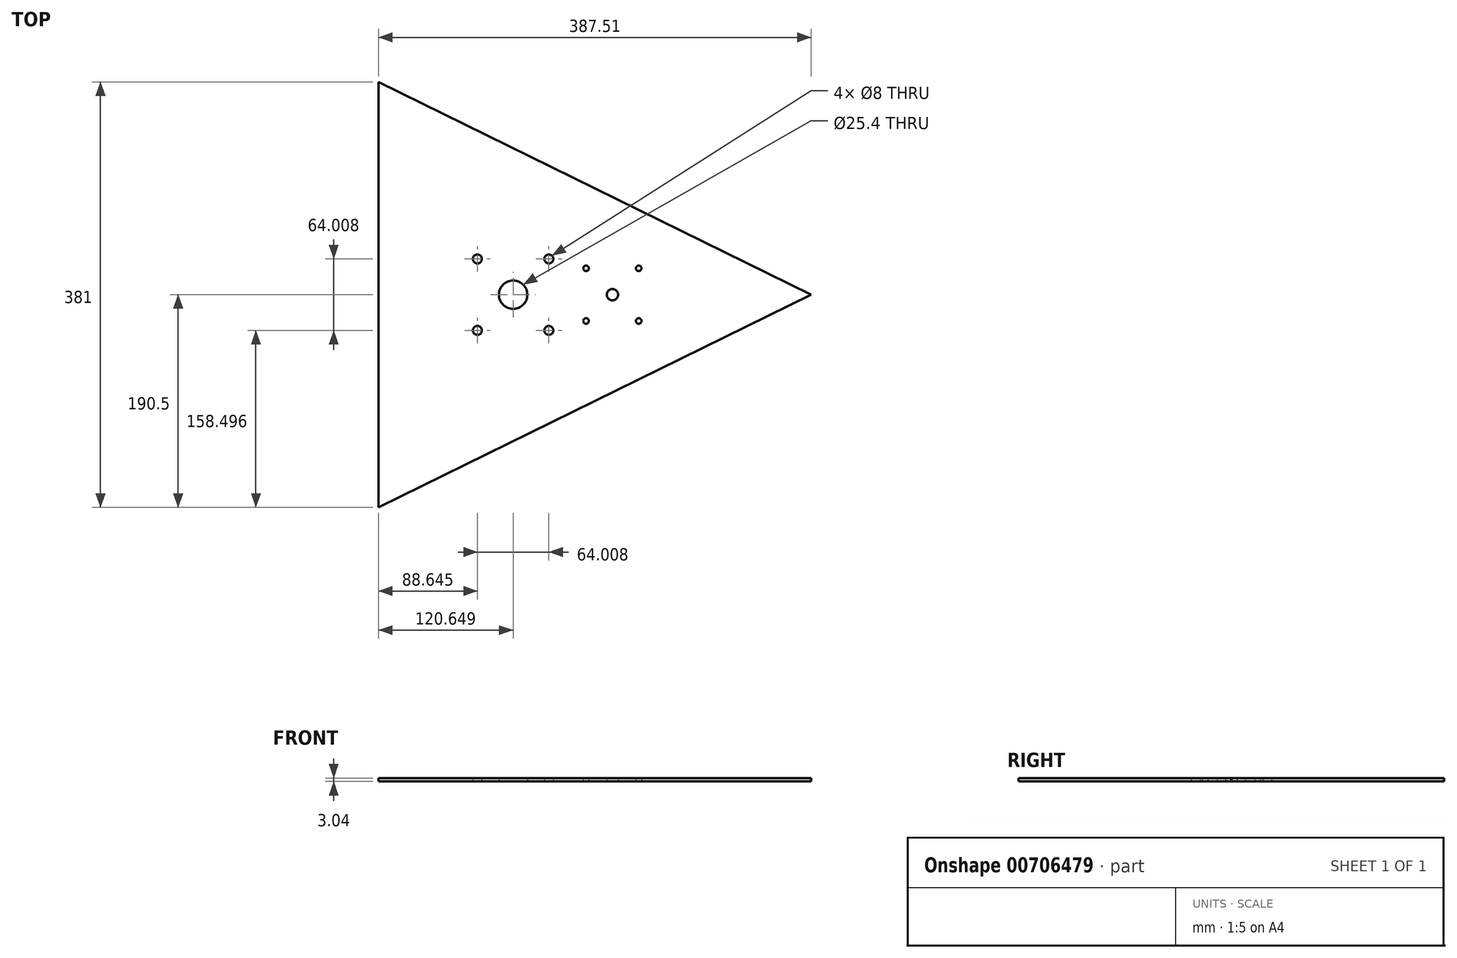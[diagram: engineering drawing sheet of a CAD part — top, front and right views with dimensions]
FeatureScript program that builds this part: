
annotation { "Feature Type Name" : "Feature", "Feature Type Description" : "" }
export const myFeature = defineFeature(function(context is Context, id is Id, definition is map)
    precondition{}
    {
        {
            var Q0;
            Q0=qCreatedBy(makeId("Top.planeOp"),FACE);
            var sketch = newSketch(context, id + "F0", { "sketchPlane" : qUnion([Q0])});
            skLineSegment(sketch, "E0.0", {"start": v(290.39, 0) * mm, "end": v(-97.12, -190.5) * mm});
            skLineSegment(sketch, "E0.1", {"start": v(-97.12, -190.5) * mm, "end": v(-97.12, 190.5) * mm});
            skLineSegment(sketch, "E0.2", {"start": v(-97.12, 190.5) * mm, "end": v(290.39, 0) * mm});
            skPoint(sketch, "E0.0.midPoint", {"position": v(76.2, 0) * mm});
            skCircle(sketch, "E1", {"center": v(88.83, 23.6) * mm, "radius": 2.48 * mm});
            skCircle(sketch, "E2", {"center": v(135.97, 23.6) * mm, "radius": 2.48 * mm});
            skCircle(sketch, "E3", {"center": v(88.83, -23.55) * mm, "radius": 2.48 * mm});
            skCircle(sketch, "E4", {"center": v(135.97, -23.55) * mm, "radius": 2.48 * mm});
            skCircle(sketch, "E5", {"center": v(112.43, 0) * mm, "radius": 5.08 * mm});
            skCircle(sketch, "E6", {"center": v(23.53, 0) * mm, "radius": 12.7 * mm});
            skCircle(sketch, "E7", {"center": v(23.53, 0) * mm, "radius": 9.53 * mm});
            skLineSegment(sketch, "E8.0", {"start": v(-95.09, 187.24) * mm, "end": v(285.78, 0) * mm, "construction": true});
            skLineSegment(sketch, "E8.1", {"start": v(-95.09, -187.24) * mm, "end": v(-95.09, 187.24) * mm, "construction": true});
            skLineSegment(sketch, "E8.2", {"start": v(285.78, 0) * mm, "end": v(-95.09, -187.24) * mm, "construction": true});
            skCircle(sketch, "E9", {"center": v(-88.74, -177.04) * mm, "radius": 6.35 * mm, "construction": true});
            skCircle(sketch, "E10", {"center": v(-88.74, 177.04) * mm, "radius": 6.35 * mm, "construction": true});
            skCircle(sketch, "E11", {"center": v(271.39, 0) * mm, "radius": 6.35 * mm, "construction": true});
            skCircle(sketch, "E12", {"center": v(-8.47, 32) * mm, "radius": 6 * mm, "construction": true});
            skCircle(sketch, "E13", {"center": v(55.53, 32) * mm, "radius": 6 * mm, "construction": true});
            skCircle(sketch, "E14", {"center": v(55.53, -32) * mm, "radius": 6 * mm, "construction": true});
            skCircle(sketch, "E15", {"center": v(-8.47, -32) * mm, "radius": 6 * mm, "construction": true});
            skLineSegment(sketch, "E16", {"start": v(290.39, 0) * mm, "end": v(-97.12, 0) * mm, "construction": true});
            skLineSegment(sketch, "E17", {"start": v(75.47, -105.65) * mm, "end": v(23.53, 0) * mm, "construction": true});
            skCircle(sketch, "E18", {"center": v(-8.47, 32) * mm, "radius": 4 * mm});
            skCircle(sketch, "E19", {"center": v(55.53, 32) * mm, "radius": 4 * mm});
            skCircle(sketch, "E20", {"center": v(-8.47, -32) * mm, "radius": 4 * mm});
            skCircle(sketch, "E21", {"center": v(55.53, -32) * mm, "radius": 4 * mm});
            skSolve(sketch);
        }
        {
            var Q0;
            Q0=qSketchRegion(id+"F0",true);
            extrude(context, id + "F1", {"entities" : qUnion([Q0]), "depth" : 3.04 * mm, "offsetDistance" : 25.4 * mm});
        }
    });
